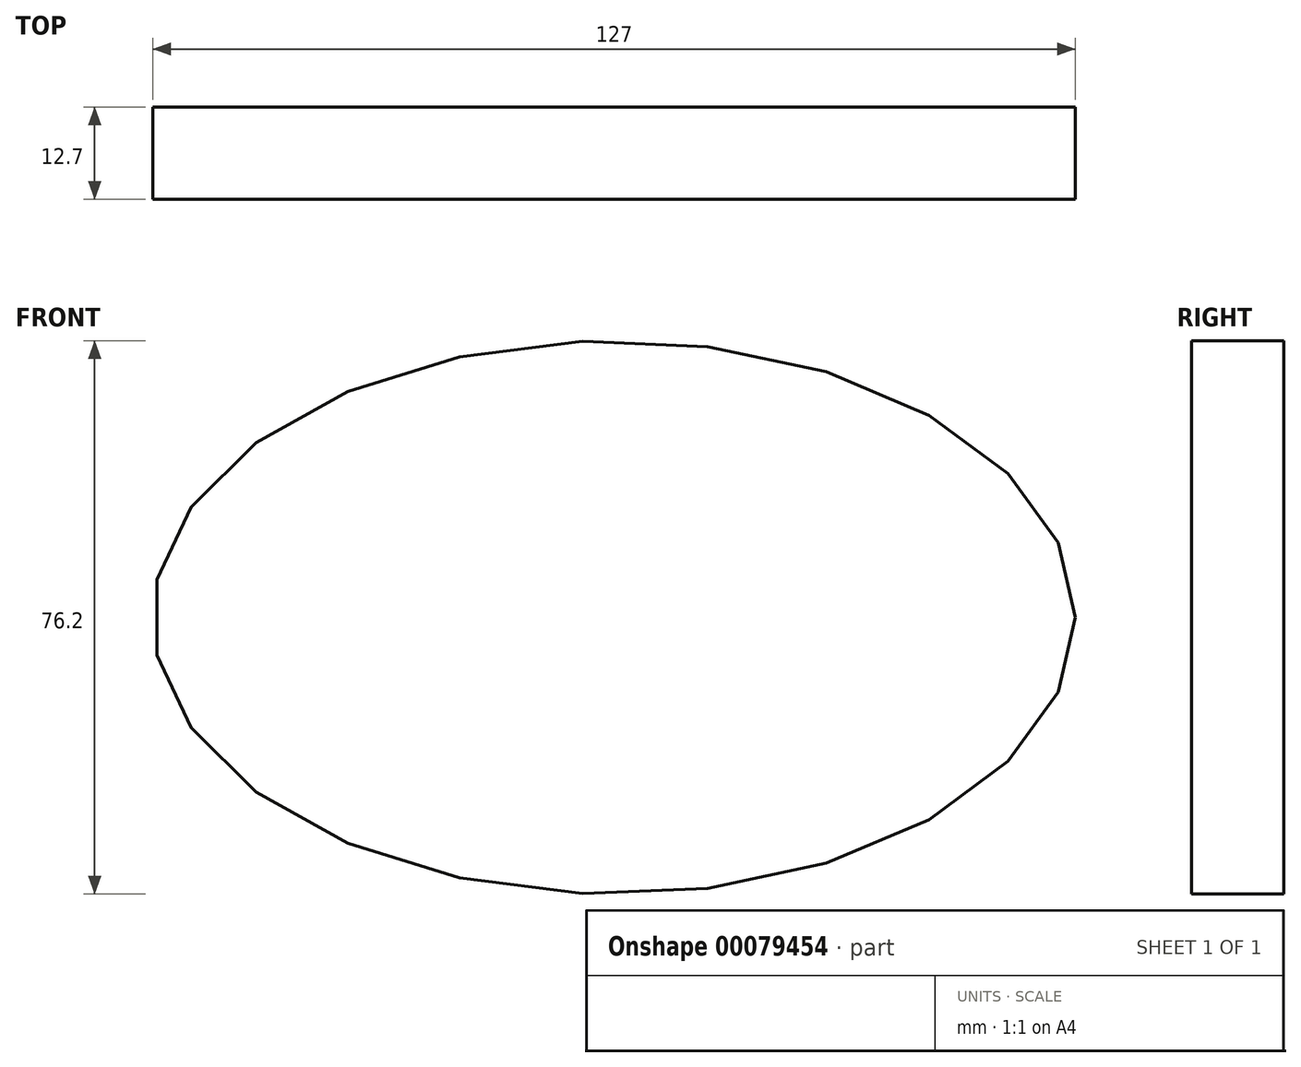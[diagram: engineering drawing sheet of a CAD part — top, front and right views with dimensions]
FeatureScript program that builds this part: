
annotation { "Feature Type Name" : "Feature", "Feature Type Description" : "" }
export const myFeature = defineFeature(function(context is Context, id is Id, definition is map)
    precondition{}
    {
        {
            var Q0;
            Q0=qCreatedBy(makeId("Front.planeOp"),FACE);
            var sketch = newSketch(context, id + "F0", { "sketchPlane" : qUnion([Q0])});
            skLineSegment(sketch, "E0", {"start": v(-63.5, 20.96) * mm, "end": v(-51.53, 20.96) * mm});
            skEllipse(sketch, "E1", {"center": v(0, 20.96) * mm, "majorRadius": 63.5 * mm, "minorRadius": 38.1 * mm, "majorAxis": v(1, 0)});
            skPoint(sketch, "E1.centerSnap0", {"position": v(5.99, 20.96) * mm});
            skLineSegment(sketch, "E2.trimOffspring", {"start": v(0, 20.96) * mm, "end": v(5.99, 20.96) * mm});
            skPoint(sketch, "E3.orphan", {"position": v(63.5, 20.96) * mm});
            skFitSpline(sketch, "E4.0", {"points": [v(57.11, 19.6) * mm, v(57.17, 20.96) * mm, v(57.11, 22.33) * mm, v(56.89, 24.14) * mm, v(56.32, 26.42) * mm, v(55.17, 29.17) * mm, v(53.53, 31.93) * mm, v(51.36, 34.69) * mm, v(48.67, 37.4) * mm, v(46, 39.57) * mm, v(43.59, 41.24) * mm, v(41.65, 42.46) * mm, v(39.6, 43.63) * mm, v(36.74, 45.11) * mm, v(32.93, 46.8) * mm, v(28.01, 48.57) * mm, v(22.8, 50.05) * mm, v(17.36, 51.22) * mm, v(11.72, 52.07) * mm, v(6.88, 52.5) * mm, v(2.96, 52.68) * mm, v(0, 52.72) * mm, v(-2.96, 52.68) * mm, v(-6.88, 52.5) * mm, v(-11.72, 52.07) * mm, v(-17.36, 51.22) * mm, v(-22.8, 50.05) * mm, v(-28.01, 48.57) * mm, v(-32.93, 46.8) * mm, v(-36.74, 45.11) * mm, v(-39.6, 43.63) * mm, v(-41.65, 42.46) * mm, v(-43.59, 41.24) * mm, v(-46, 39.57) * mm, v(-48.67, 37.4) * mm, v(-51.36, 34.69) * mm, v(-53.53, 31.93) * mm, v(-55.17, 29.17) * mm, v(-56.32, 26.42) * mm, v(-56.89, 24.14) * mm, v(-57.11, 22.33) * mm, v(-57.17, 20.96) * mm, v(-57.11, 19.6) * mm, v(-56.89, 17.78) * mm, v(-56.32, 15.5) * mm, v(-55.17, 12.75) * mm, v(-53.53, 9.98) * mm, v(-51.36, 7.23) * mm, v(-48.67, 4.53) * mm, v(-46, 2.35) * mm, v(-43.59, 0.67) * mm, v(-41.65, -0.54) * mm, v(-39.6, -1.71) * mm, v(-36.74, -3.2) * mm, v(-32.93, -4.89) * mm, v(-28.01, -6.65) * mm, v(-22.8, -8.13) * mm, v(-17.36, -9.3) * mm, v(-11.72, -10.15) * mm, v(-6.88, -10.59) * mm, v(-2.96, -10.76) * mm, v(0, -10.8) * mm, v(2.96, -10.76) * mm, v(6.88, -10.59) * mm, v(11.72, -10.15) * mm, v(17.36, -9.3) * mm, v(22.8, -8.13) * mm, v(28.01, -6.65) * mm, v(32.93, -4.89) * mm, v(36.74, -3.2) * mm, v(39.6, -1.71) * mm, v(41.65, -0.54) * mm, v(43.59, 0.67) * mm, v(46, 2.35) * mm, v(48.67, 4.53) * mm, v(51.36, 7.23) * mm, v(53.53, 9.98) * mm, v(55.17, 12.75) * mm, v(56.32, 15.5) * mm, v(56.89, 17.78) * mm, v(57.11, 19.6) * mm, v(57.17, 20.96) * mm, v(57.11, 22.33) * mm, v(57.11, 19.6) * mm]});
            skSolve(sketch);
        }
        {
            var Q0;
            Q0=qSketchRegion(id+"F0",true);
            extrude(context, id + "F1", {"entities" : qUnion([Q0]), "depth" : 12.7 * mm});
        }
    });
